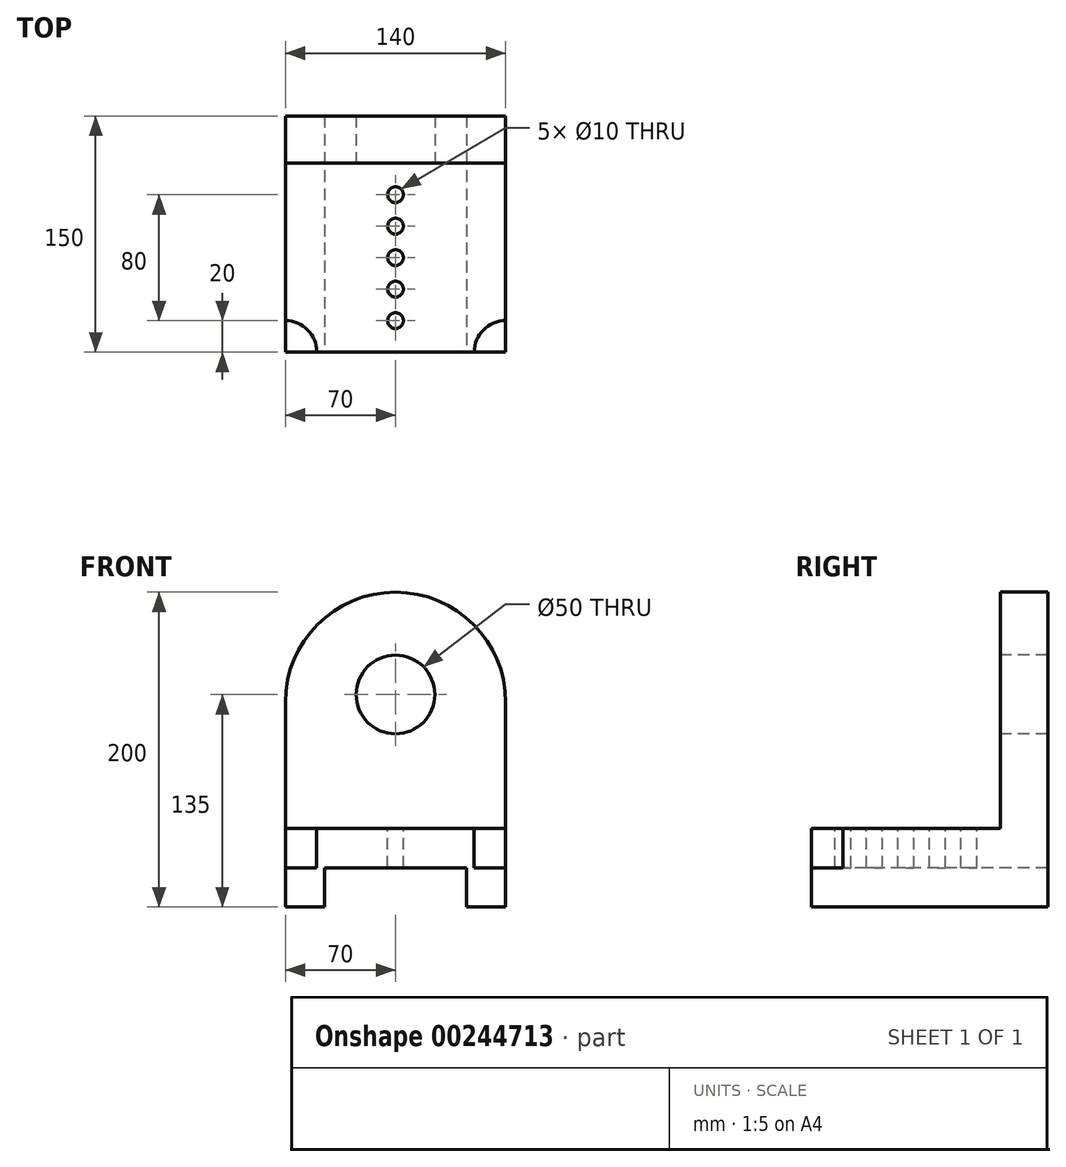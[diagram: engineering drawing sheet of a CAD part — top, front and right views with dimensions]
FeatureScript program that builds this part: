
annotation { "Feature Type Name" : "Feature", "Feature Type Description" : "" }
export const myFeature = defineFeature(function(context is Context, id is Id, definition is map)
    precondition{}
    {
        {
            var Q0;
            Q0=qCreatedBy(makeId("Front.planeOp"),FACE);
            var sketch = newSketch(context, id + "F0", { "sketchPlane" : qUnion([Q0])});
            skLineSegment(sketch, "E0.bottom", {"start": v(70, 87.5) * mm, "end": v(-70, 87.5) * mm});
            skLineSegment(sketch, "E0.top", {"start": v(70, -87.5) * mm, "end": v(-70, -87.5) * mm});
            skLineSegment(sketch, "E0.left", {"start": v(70, 87.5) * mm, "end": v(70, -87.5) * mm});
            skLineSegment(sketch, "E0.right", {"start": v(-70, 87.5) * mm, "end": v(-70, -87.5) * mm});
            skPoint(sketch, "E0.middle", {"position": v(0, 0) * mm});
            skSolve(sketch);
        }
        {
            var Q0;
            Q0 = qSketchRegion(id + "F0", true);
            extrude(context, id + "F1", {"entities" : qUnion([Q0]), "depth" : 30 * mm});
        }
        {
            var Q0;
            Q0=makeQuery(id+"F1.opExtrude","SWEPT_EDGE",EDGE,{"disambiguationData":[OSD([sQuery(id+"F0.wireOp",EDGE,"E0.bottom"),sQuery(id+"F0.wireOp",EDGE,"E0.left")])]});
            var Q1;
            Q1=makeQuery(id+"F1.opExtrude","SWEPT_EDGE",EDGE,{"disambiguationData":[OSD([sQuery(id+"F0.wireOp",EDGE,"E0.bottom"),sQuery(id+"F0.wireOp",EDGE,"E0.right")])]});
            fillet(context, id + "F2", {"entities" : qUnion([Q0, Q1]), "radius" : 70 * mm, "tangentPropagation" : true, "allowEdgeOverflow" : false});
        }
        {
            var Q0;
            Q0=makeQuery(id+"F1.opExtrude","CAP_FACE",FACE,{"disambiguationData":[OSD([sQuery(id+"F0.wireOp",EDGE,"E0.bottom"),sQuery(id+"F0.wireOp",EDGE,"E0.top"),sQuery(id+"F0.wireOp",EDGE,"E0.left"),sQuery(id+"F0.wireOp",EDGE,"E0.right")])],"isStart":false});
            var sketch = newSketch(context, id + "F3", { "sketchPlane" : qUnion([Q0])});
            skCircle(sketch, "E1", {"center": v(0, 22.5) * mm, "radius": 25 * mm});
            skSolve(sketch);
        }
        {
            var Q0;
            Q0 = qSketchRegion(id + "F3", true);
            extrude(context, id + "F4", {"entities" : qUnion([Q0]), "operationType" : NewBodyOperationType.REMOVE, "endBound" : BoundingType.THROUGH_ALL, "oppositeDirection" : true, "depth" : 25.4 * mm});
        }
        {
            var Q0;
            Q0=makeQuery(id+"F1.opExtrude","CAP_FACE",FACE,{"disambiguationData":[OSD([sQuery(id+"F0.wireOp",EDGE,"E0.bottom"),sQuery(id+"F0.wireOp",EDGE,"E0.top"),sQuery(id+"F0.wireOp",EDGE,"E0.left"),sQuery(id+"F0.wireOp",EDGE,"E0.right")])],"isStart":false});
            var sketch = newSketch(context, id + "F5", { "sketchPlane" : qUnion([Q0])});
            skLineSegment(sketch, "E2.bottom", {"start": v(-70, -87.5) * mm, "end": v(70, -87.5) * mm});
            skLineSegment(sketch, "E2.top", {"start": v(-70, -62.5) * mm, "end": v(70, -62.5) * mm});
            skLineSegment(sketch, "E2.left", {"start": v(-70, -87.5) * mm, "end": v(-70, -62.5) * mm});
            skLineSegment(sketch, "E2.right", {"start": v(70, -87.5) * mm, "end": v(70, -62.5) * mm});
            skSolve(sketch);
        }
        {
            var Q0;
            Q0 = qSketchRegion(id + "F5", true);
            extrude(context, id + "F6", {"entities" : qUnion([Q0]), "operationType" : NewBodyOperationType.ADD, "depth" : 120 * mm});
        }
        {
            var Q0;
            Q0=makeQuery(id+"F6.boolean.opBoolean","MERGE",FACE,{"derivedFrom":[makeQuery(id+"F1.opExtrude","SWEPT_FACE",FACE,{"disambiguationData":[OSD([sQuery(id+"F0.wireOp",EDGE,"E0.top")])]}),makeQuery(id+"F6.opExtrude","SWEPT_FACE",FACE,{"disambiguationData":[OSD([sQuery(id+"F5.wireOp",EDGE,"E2.bottom")])]})]});
            var sketch = newSketch(context, id + "F7", { "sketchPlane" : qUnion([Q0])});
            skLineSegment(sketch, "E3.bottom", {"start": v(-70, 0) * mm, "end": v(-45, 0) * mm});
            skLineSegment(sketch, "E3.top", {"start": v(-70, 150) * mm, "end": v(-45, 150) * mm});
            skLineSegment(sketch, "E3.left", {"start": v(-70, 0) * mm, "end": v(-70, 150) * mm});
            skLineSegment(sketch, "E3.right", {"start": v(-45, 0) * mm, "end": v(-45, 150) * mm});
            skLineSegment(sketch, "E4.bottom", {"start": v(70, 0) * mm, "end": v(45, 0) * mm});
            skLineSegment(sketch, "E4.top", {"start": v(70, 150) * mm, "end": v(45, 150) * mm});
            skLineSegment(sketch, "E4.left", {"start": v(70, 0) * mm, "end": v(70, 150) * mm});
            skLineSegment(sketch, "E4.right", {"start": v(45, 0) * mm, "end": v(45, 150) * mm});
            skSolve(sketch);
        }
        {
            var Q0;
            Q0 = qSketchRegion(id + "F7", true);
            extrude(context, id + "F8", {"entities" : qUnion([Q0]), "operationType" : NewBodyOperationType.ADD, "depth" : 25 * mm});
        }
        {
            var Q0;
            Q0=makeQuery(id+"F6.opExtrude","SWEPT_FACE",FACE,{"disambiguationData":[OSD([sQuery(id+"F5.wireOp",EDGE,"E2.top")])]});
            var sketch = newSketch(context, id + "F9", { "sketchPlane" : qUnion([Q0])});
            skCircle(sketch, "E5", {"center": v(-70, -150) * mm, "radius": 20 * mm});
            skCircle(sketch, "E6", {"center": v(70, -150) * mm, "radius": 20 * mm});
            skSolve(sketch);
        }
        {
            var Q0;
            Q0 = qSketchRegion(id + "F9", true);
            extrude(context, id + "F10", {"entities" : qUnion([Q0]), "operationType" : NewBodyOperationType.REMOVE, "oppositeDirection" : true, "depth" : 25 * mm});
        }
        {
            var Q0;
            Q0=makeQuery(id+"F6.opExtrude","SWEPT_FACE",FACE,{"disambiguationData":[OSD([sQuery(id+"F5.wireOp",EDGE,"E2.top")])]});
            var sketch = newSketch(context, id + "F11", { "sketchPlane" : qUnion([Q0])});
            skCircle(sketch, "E7", {"center": v(0, -130) * mm, "radius": 5 * mm});
            skPoint(sketch, "E7.centerSnap0", {"position": v(0, -150) * mm});
            skCircle(sketch, "E8", {"center": v(0, -110) * mm, "radius": 5 * mm});
            skCircle(sketch, "E9", {"center": v(0, -90) * mm, "radius": 5 * mm});
            skCircle(sketch, "E10", {"center": v(0, -70) * mm, "radius": 5 * mm});
            skCircle(sketch, "E11", {"center": v(0, -50) * mm, "radius": 5 * mm});
            skSolve(sketch);
        }
        {
            var Q0;
            Q0 = qSketchRegion(id + "F11", true);
            extrude(context, id + "F12", {"entities" : qUnion([Q0]), "operationType" : NewBodyOperationType.REMOVE, "endBound" : BoundingType.THROUGH_ALL, "oppositeDirection" : true, "depth" : 25.4 * mm});
        }
    });
